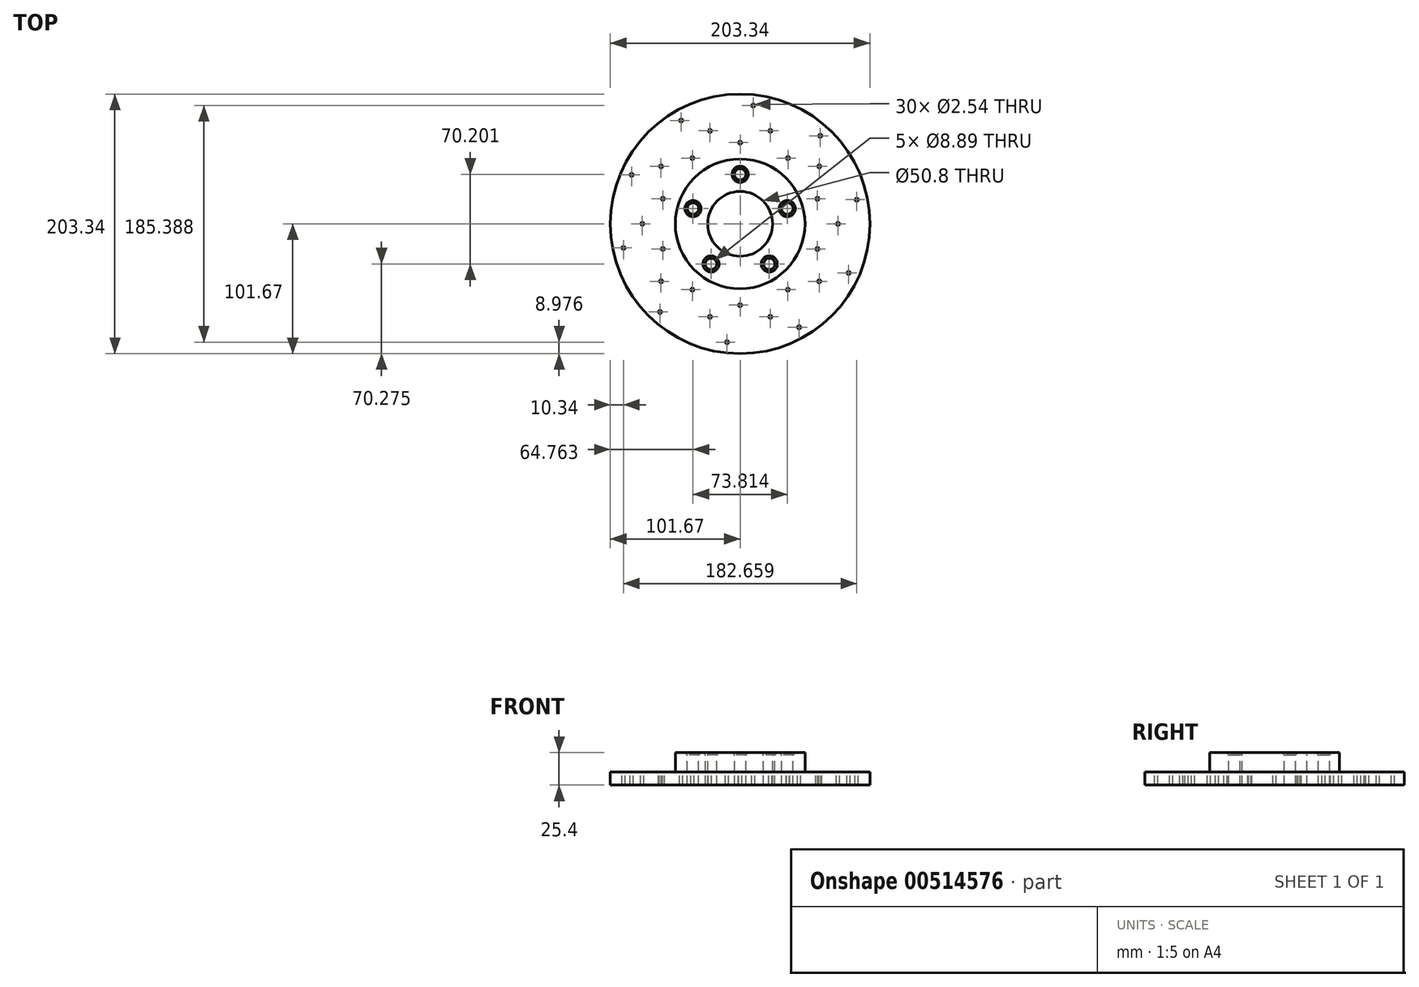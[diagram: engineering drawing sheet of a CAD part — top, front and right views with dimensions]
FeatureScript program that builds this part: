
annotation { "Feature Type Name" : "Feature", "Feature Type Description" : "" }
export const myFeature = defineFeature(function(context is Context, id is Id, definition is map)
    precondition{}
    {
        {
            var Q0;
            Q0=qCreatedBy(makeId("Top.planeOp"),FACE);
            var sketch = newSketch(context, id + "F0", { "sketchPlane" : qUnion([Q0])});
            skCircle(sketch, "E0", {"center": v(0, 0) * mm, "radius": 101.67 * mm});
            skSolve(sketch);
        }
        {
            var Q0;
            Q0=makeQuery(id+"F0.imprint","IMPRINT",FACE,{"disambiguationData":[TD([[makeQuery(id+"F0.imprint","IMPRINT",EDGE,{"derivedFrom":sQuery(id+"F0.wireOp",EDGE,"E0")}),1.0]])]});
            extrude(context, id + "F1", {"entities" : qUnion([Q0]), "depth" : 10.16 * mm, "offsetDistance" : 25.4 * mm});
        }
        {
            var Q0;
            Q0=makeQuery(id+"F1.opExtrude","CAP_FACE",FACE,{"disambiguationData":[OSD([sQuery(id+"F0.wireOp",EDGE,"E0")])],"isStart":false});
            var sketch = newSketch(context, id + "F2", { "sketchPlane" : qUnion([Q0])});
            skCircle(sketch, "E1", {"center": v(0, 0) * mm, "radius": 50.83 * mm});
            skSolve(sketch);
        }
        {
            var Q0;
            Q0=makeQuery(id+"F2.imprint","IMPRINT",FACE,{"disambiguationData":[TD([[makeQuery(id+"F2.imprint","IMPRINT",EDGE,{"derivedFrom":sQuery(id+"F2.wireOp",EDGE,"E1")}),1.0]])]});
            var Q1;
            Q1=sQuery(id+"F2.wireOp",EDGE,"E1");
            extrude(context, id + "F3", {"entities" : qUnion([Q0]), "operationType" : NewBodyOperationType.ADD, "surfaceEntities" : qUnion([Q1]), "depth" : 15.24 * mm, "offsetDistance" : 25.4 * mm});
        }
        {
            var Q0;
            Q0=makeQuery(id+"F3.opExtrude","CAP_FACE",FACE,{"disambiguationData":[OSD([sQuery(id+"F2.wireOp",EDGE,"E1")])],"isStart":false});
            var sketch = newSketch(context, id + "F4", { "sketchPlane" : qUnion([Q0])});
            skPoint(sketch, "E2", {"position": v(0, 0) * mm});
            skSolve(sketch);
        }
        {
            var Q0;
            Q0=sQuery(id+"F4.wireOp",VERTEX,"E2");
            var Q1;
            Q1=makeQuery(id+"F1.opExtrude","SWEPT_BODY",BODY,{"disambiguationData":[OSD([sQuery(id+"F0.wireOp",EDGE,"E0")])]});
            hole(context, id + "F5", {"style" : HoleStyle.SIMPLE, "endStyle" : HoleEndStyle.THROUGH, "holeDiameter" : 50.8 * mm, "isTappedThrough" : true, "tappedDepth" : 12.7 * mm, "tapClearance" : 3, "locations" : qUnion([Q0]), "scope" : qUnion([Q1])});
        }
        {
            var Q0;
            Q0=makeQuery(id+"F3.opExtrude","CAP_FACE",FACE,{"disambiguationData":[OSD([sQuery(id+"F2.wireOp",EDGE,"E1")])],"isStart":false});
            var sketch = newSketch(context, id + "F6", { "sketchPlane" : qUnion([Q0])});
            skCircle(sketch, "E3.cCircle", {"center": v(0, 0) * mm, "radius": 38.8 * mm, "construction": true});
            skLineSegment(sketch, "E3.0", {"start": v(0, 38.8) * mm, "end": v(36.9, 12) * mm});
            skLineSegment(sketch, "E3.1", {"start": v(36.9, 12) * mm, "end": v(22.8, -31.4) * mm});
            skLineSegment(sketch, "E3.2", {"start": v(22.8, -31.4) * mm, "end": v(-22.8, -31.4) * mm});
            skLineSegment(sketch, "E3.3", {"start": v(-22.8, -31.4) * mm, "end": v(-36.9, 12) * mm});
            skLineSegment(sketch, "E3.4", {"start": v(-36.9, 12) * mm, "end": v(0, 38.8) * mm});
            skPoint(sketch, "E4", {"position": v(0, 38.8) * mm});
            skPoint(sketch, "E5", {"position": v(-36.9, 12) * mm});
            skPoint(sketch, "E6", {"position": v(-22.8, -31.4) * mm});
            skPoint(sketch, "E7", {"position": v(22.8, -31.4) * mm});
            skPoint(sketch, "E8", {"position": v(36.9, 12) * mm});
            skSolve(sketch);
        }
        {
            var Q0;
            Q0=sQuery(id+"F6.wireOp",VERTEX,"E4");
            var Q1;
            Q1=sQuery(id+"F6.wireOp",VERTEX,"E5");
            var Q2;
            Q2=sQuery(id+"F6.wireOp",VERTEX,"E6");
            var Q3;
            Q3=sQuery(id+"F6.wireOp",VERTEX,"E7");
            var Q4;
            Q4=sQuery(id+"F6.wireOp",VERTEX,"E8");
            var Q5;
            Q5=makeQuery(id+"F1.opExtrude","SWEPT_BODY",BODY,{"disambiguationData":[OSD([sQuery(id+"F0.wireOp",EDGE,"E0")])]});
            hole(context, id + "F7", {"style" : HoleStyle.C_SINK, "endStyle" : HoleEndStyle.THROUGH, "holeDiameter" : 8.9 * mm, "cSinkDiameter" : 12.7 * mm, "cSinkAngle" : 90 * degree, "isTappedThrough" : true, "tappedDepth" : 12.7 * mm, "tapClearance" : 3, "locations" : qUnion([Q0, Q1, Q2, Q3, Q4]), "scope" : qUnion([Q5])});
        }
        {
            var Q0;
            Q0=makeQuery(id+"F1.opExtrude","CAP_FACE",FACE,{"disambiguationData":[OSD([sQuery(id+"F0.wireOp",EDGE,"E0")])],"isStart":false});
            var sketch = newSketch(context, id + "F8", { "sketchPlane" : qUnion([Q0])});
            skCircle(sketch, "E9.cCircle", {"center": v(0, 0) * mm, "radius": 72.85 * mm, "construction": true});
            skLineSegment(sketch, "E9.0", {"start": v(-23.67, 72.85) * mm, "end": v(23.67, 72.85) * mm});
            skLineSegment(sketch, "E9.1", {"start": v(23.67, 72.85) * mm, "end": v(61.97, 45.02) * mm});
            skLineSegment(sketch, "E9.2", {"start": v(61.97, 45.02) * mm, "end": v(76.6, 0) * mm});
            skLineSegment(sketch, "E9.3", {"start": v(76.6, 0) * mm, "end": v(61.97, -45.02) * mm});
            skLineSegment(sketch, "E9.4", {"start": v(61.97, -45.02) * mm, "end": v(23.67, -72.85) * mm});
            skLineSegment(sketch, "E9.5", {"start": v(23.67, -72.85) * mm, "end": v(-23.67, -72.85) * mm});
            skLineSegment(sketch, "E9.6", {"start": v(-23.67, -72.85) * mm, "end": v(-61.97, -45.02) * mm});
            skLineSegment(sketch, "E9.7", {"start": v(-61.97, -45.02) * mm, "end": v(-76.6, 0) * mm});
            skLineSegment(sketch, "E9.8", {"start": v(-76.6, 0) * mm, "end": v(-61.97, 45.02) * mm});
            skLineSegment(sketch, "E9.9", {"start": v(-61.97, 45.02) * mm, "end": v(-23.67, 72.85) * mm});
            skPoint(sketch, "E9.0.midPoint", {"position": v(0, 72.85) * mm});
            skCircle(sketch, "E10.cCircle", {"center": v(0, 0) * mm, "radius": 88.7 * mm, "construction": true});
            skLineSegment(sketch, "E10.0", {"start": v(-46.18, 81.03) * mm, "end": v(10.27, 92.7) * mm});
            skLineSegment(sketch, "E10.1", {"start": v(10.27, 92.7) * mm, "end": v(62.79, 68.96) * mm});
            skLineSegment(sketch, "E10.2", {"start": v(62.79, 68.96) * mm, "end": v(91.33, 18.88) * mm});
            skLineSegment(sketch, "E10.3", {"start": v(91.33, 18.88) * mm, "end": v(84.98, -38.4) * mm});
            skLineSegment(sketch, "E10.4", {"start": v(84.98, -38.4) * mm, "end": v(46.18, -81.03) * mm});
            skLineSegment(sketch, "E10.5", {"start": v(46.18, -81.03) * mm, "end": v(-10.27, -92.7) * mm});
            skLineSegment(sketch, "E10.6", {"start": v(-10.27, -92.7) * mm, "end": v(-62.79, -68.96) * mm});
            skLineSegment(sketch, "E10.7", {"start": v(-62.79, -68.96) * mm, "end": v(-91.33, -18.88) * mm});
            skLineSegment(sketch, "E10.8", {"start": v(-91.33, -18.88) * mm, "end": v(-84.98, 38.4) * mm});
            skLineSegment(sketch, "E10.9", {"start": v(-84.98, 38.4) * mm, "end": v(-46.18, 81.03) * mm});
            skPoint(sketch, "E10.0.midPoint", {"position": v(-17.96, 86.86) * mm});
            skCircle(sketch, "E11.cCircle", {"center": v(0, 0) * mm, "radius": 60.55 * mm, "construction": true});
            skLineSegment(sketch, "E11.0", {"start": v(0.03, 63.67) * mm, "end": v(37.45, 51.49) * mm});
            skLineSegment(sketch, "E11.1", {"start": v(37.45, 51.49) * mm, "end": v(60.56, 19.64) * mm});
            skLineSegment(sketch, "E11.2", {"start": v(60.56, 19.64) * mm, "end": v(60.54, -19.7) * mm});
            skLineSegment(sketch, "E11.3", {"start": v(60.54, -19.7) * mm, "end": v(37.4, -51.53) * mm});
            skLineSegment(sketch, "E11.4", {"start": v(37.4, -51.53) * mm, "end": v(-0.03, -63.67) * mm});
            skLineSegment(sketch, "E11.5", {"start": v(-0.03, -63.67) * mm, "end": v(-37.45, -51.49) * mm});
            skLineSegment(sketch, "E11.6", {"start": v(-37.45, -51.49) * mm, "end": v(-60.56, -19.64) * mm});
            skLineSegment(sketch, "E11.7", {"start": v(-60.56, -19.64) * mm, "end": v(-60.54, 19.7) * mm});
            skLineSegment(sketch, "E11.8", {"start": v(-60.54, 19.7) * mm, "end": v(-37.4, 51.53) * mm});
            skLineSegment(sketch, "E11.9", {"start": v(-37.4, 51.53) * mm, "end": v(0.03, 63.67) * mm});
            skPoint(sketch, "E11.0.midPoint", {"position": v(18.74, 57.58) * mm});
            skPoint(sketch, "E12", {"position": v(10.27, 92.7) * mm});
            skPoint(sketch, "E13", {"position": v(23.67, 72.85) * mm});
            skPoint(sketch, "E14", {"position": v(37.45, 51.49) * mm});
            skPoint(sketch, "E15", {"position": v(0.03, 63.67) * mm});
            skPoint(sketch, "E16", {"position": v(-23.67, 72.85) * mm});
            skPoint(sketch, "E17", {"position": v(-46.18, 81.03) * mm});
            skPoint(sketch, "E18", {"position": v(-37.4, 51.53) * mm});
            skPoint(sketch, "E19", {"position": v(-61.97, 45.02) * mm});
            skPoint(sketch, "E20", {"position": v(-84.98, 38.4) * mm});
            skPoint(sketch, "E21", {"position": v(-60.54, 19.7) * mm});
            skPoint(sketch, "E22", {"position": v(-76.6, 0) * mm});
            skPoint(sketch, "E23", {"position": v(-91.33, -18.88) * mm});
            skPoint(sketch, "E24", {"position": v(-62.79, -68.96) * mm});
            skPoint(sketch, "E25", {"position": v(-61.97, -45.02) * mm});
            skPoint(sketch, "E26", {"position": v(-60.56, -19.64) * mm});
            skPoint(sketch, "E27", {"position": v(-37.45, -51.49) * mm});
            skPoint(sketch, "E28", {"position": v(-23.67, -72.85) * mm});
            skPoint(sketch, "E29", {"position": v(-10.27, -92.7) * mm});
            skPoint(sketch, "E30", {"position": v(-0.03, -63.67) * mm});
            skPoint(sketch, "E31", {"position": v(23.67, -72.85) * mm});
            skPoint(sketch, "E32", {"position": v(46.18, -81.03) * mm});
            skPoint(sketch, "E33", {"position": v(37.4, -51.53) * mm});
            skPoint(sketch, "E34", {"position": v(61.97, -45.02) * mm});
            skPoint(sketch, "E35", {"position": v(84.98, -38.4) * mm});
            skPoint(sketch, "E36", {"position": v(60.54, -19.7) * mm});
            skPoint(sketch, "E37", {"position": v(76.6, 0) * mm});
            skPoint(sketch, "E38", {"position": v(91.33, 18.88) * mm});
            skPoint(sketch, "E39", {"position": v(60.56, 19.64) * mm});
            skPoint(sketch, "E40", {"position": v(61.97, 45.02) * mm});
            skPoint(sketch, "E41", {"position": v(62.79, 68.96) * mm});
            skSolve(sketch);
        }
        {
            var Q0;
            Q0=sQuery(id+"F8.wireOp",VERTEX,"E12");
            var Q1;
            Q1=sQuery(id+"F8.wireOp",VERTEX,"E17");
            var Q2;
            Q2=sQuery(id+"F8.wireOp",VERTEX,"E16");
            var Q3;
            Q3=sQuery(id+"F8.wireOp",VERTEX,"E15");
            var Q4;
            Q4=sQuery(id+"F8.wireOp",VERTEX,"E13");
            var Q5;
            Q5=sQuery(id+"F8.wireOp",VERTEX,"E14");
            var Q6;
            Q6=sQuery(id+"F8.wireOp",VERTEX,"E41");
            var Q7;
            Q7=sQuery(id+"F8.wireOp",VERTEX,"E40");
            var Q8;
            Q8=sQuery(id+"F8.wireOp",VERTEX,"E39");
            var Q9;
            Q9=sQuery(id+"F8.wireOp",VERTEX,"E38");
            var Q10;
            Q10=sQuery(id+"F8.wireOp",VERTEX,"E37");
            var Q11;
            Q11=sQuery(id+"F8.wireOp",VERTEX,"E36");
            var Q12;
            Q12=sQuery(id+"F8.wireOp",VERTEX,"E35");
            var Q13;
            Q13=sQuery(id+"F8.wireOp",VERTEX,"E34");
            var Q14;
            Q14=sQuery(id+"F8.wireOp",VERTEX,"E33");
            var Q15;
            Q15=sQuery(id+"F8.wireOp",VERTEX,"E32");
            var Q16;
            Q16=sQuery(id+"F8.wireOp",VERTEX,"E31");
            var Q17;
            Q17=sQuery(id+"F8.wireOp",VERTEX,"E30");
            var Q18;
            Q18=sQuery(id+"F8.wireOp",VERTEX,"E29");
            var Q19;
            Q19=sQuery(id+"F8.wireOp",VERTEX,"E28");
            var Q20;
            Q20=sQuery(id+"F8.wireOp",VERTEX,"E27");
            var Q21;
            Q21=sQuery(id+"F8.wireOp",VERTEX,"E24");
            var Q22;
            Q22=sQuery(id+"F8.wireOp",VERTEX,"E25");
            var Q23;
            Q23=sQuery(id+"F8.wireOp",VERTEX,"E26");
            var Q24;
            Q24=sQuery(id+"F8.wireOp",VERTEX,"E23");
            var Q25;
            Q25=sQuery(id+"F8.wireOp",VERTEX,"E22");
            var Q26;
            Q26=sQuery(id+"F8.wireOp",VERTEX,"E21");
            var Q27;
            Q27=sQuery(id+"F8.wireOp",VERTEX,"E20");
            var Q28;
            Q28=sQuery(id+"F8.wireOp",VERTEX,"E19");
            var Q29;
            Q29=sQuery(id+"F8.wireOp",VERTEX,"E18");
            var Q30;
            Q30=makeQuery(id+"F1.opExtrude","SWEPT_BODY",BODY,{"disambiguationData":[OSD([sQuery(id+"F0.wireOp",EDGE,"E0")])]});
            hole(context, id + "F9", {"style" : HoleStyle.SIMPLE, "endStyle" : HoleEndStyle.THROUGH, "holeDiameter" : 2.54 * mm, "isTappedThrough" : true, "tappedDepth" : 12.7 * mm, "tapClearance" : 3, "locations" : qUnion([Q0, Q1, Q2, Q3, Q4, Q5, Q6, Q7, Q8, Q9, Q10, Q11, Q12, Q13, Q14, Q15, Q16, Q17, Q18, Q19, Q20, Q21, Q22, Q23, Q24, Q25, Q26, Q27, Q28, Q29]), "scope" : qUnion([Q30])});
        }
    });
